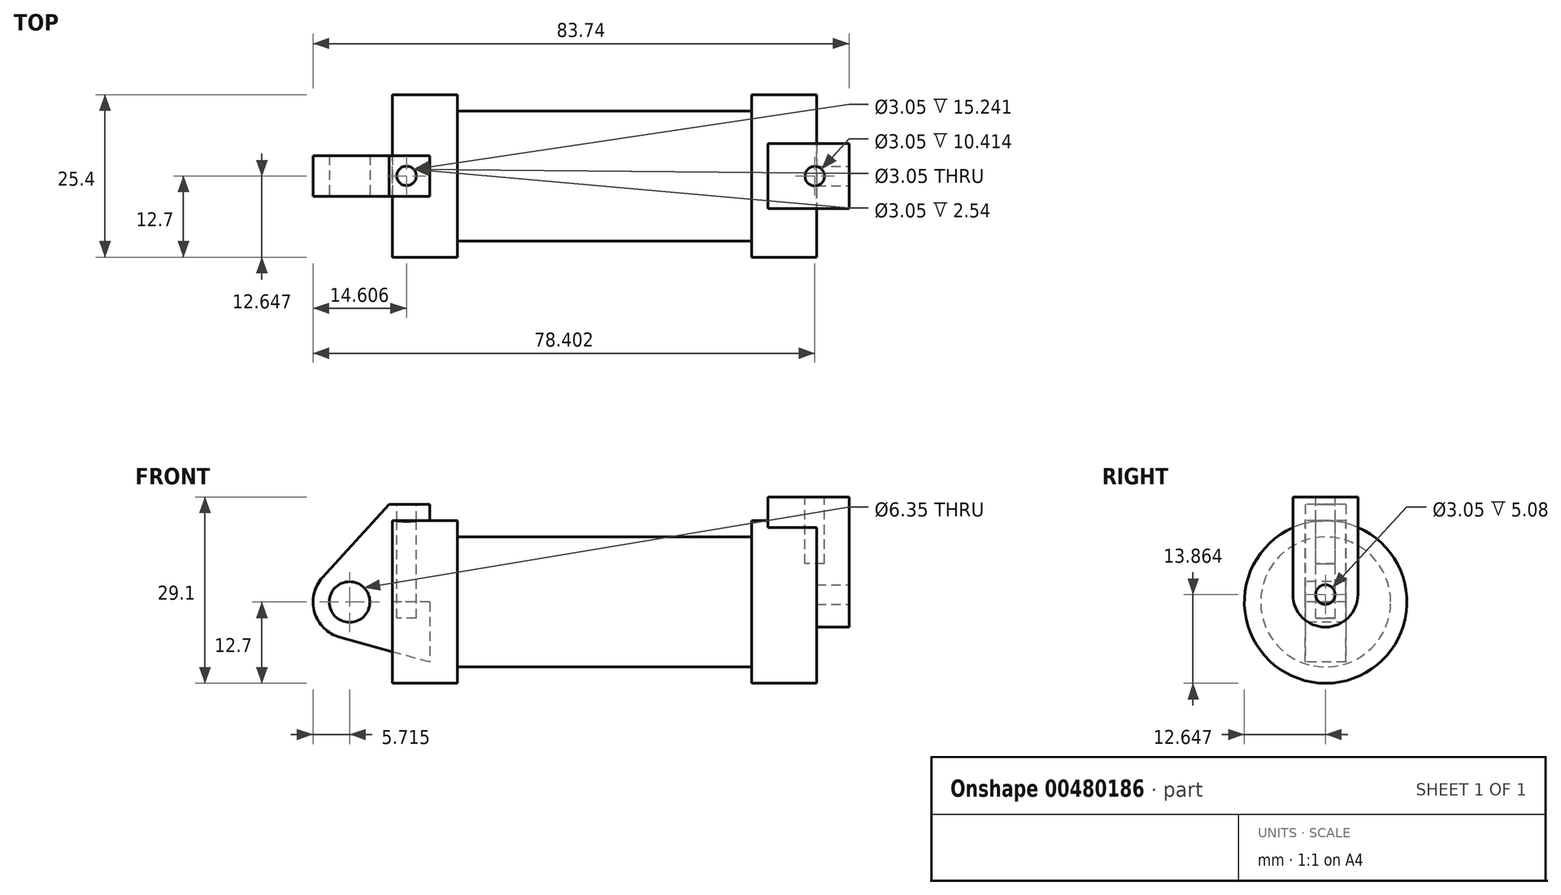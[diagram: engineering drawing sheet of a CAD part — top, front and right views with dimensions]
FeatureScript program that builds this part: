
annotation { "Feature Type Name" : "Feature", "Feature Type Description" : "" }
export const myFeature = defineFeature(function(context is Context, id is Id, definition is map)
    precondition{}
    {
        {
            var Q0;
            Q0=qCreatedBy(makeId("Front.planeOp"),FACE);
            var sketch = newSketch(context, id + "F0", { "sketchPlane" : qUnion([Q0])});
            skLineSegment(sketch, "E0", {"start": v(0, 0) * mm, "end": v(0, 12.7) * mm});
            skLineSegment(sketch, "E1", {"start": v(0, 12.7) * mm, "end": v(10.16, 12.7) * mm});
            skLineSegment(sketch, "E2", {"start": v(10.16, 12.7) * mm, "end": v(10.16, 10.16) * mm});
            skLineSegment(sketch, "E3", {"start": v(10.16, 10.16) * mm, "end": v(56.13, 10.16) * mm});
            skLineSegment(sketch, "E4", {"start": v(56.13, 10.16) * mm, "end": v(56.13, 12.7) * mm});
            skLineSegment(sketch, "E5", {"start": v(56.13, 12.7) * mm, "end": v(66.3, 12.7) * mm});
            skLineSegment(sketch, "E6", {"start": v(66.3, 12.7) * mm, "end": v(66.3, 0) * mm});
            skLineSegment(sketch, "E7", {"start": v(66.3, 0) * mm, "end": v(0, 0) * mm});
            skLineSegment(sketch, "E8", {"start": v(5.84, 15.24) * mm, "end": v(-0.5, 15.24) * mm});
            skLineSegment(sketch, "E9", {"start": v(-0.5, 15.24) * mm, "end": v(-10.88, 3.85) * mm});
            skLineSegment(sketch, "E10", {"start": v(0, 0) * mm, "end": v(-6.65, 0) * mm});
            skCircle(sketch, "E11", {"center": v(-6.65, 0) * mm, "radius": 5.72 * mm});
            skCircle(sketch, "E12", {"center": v(-6.65, 0) * mm, "radius": 3.18 * mm});
            skLineSegment(sketch, "E13", {"start": v(5.84, 15.24) * mm, "end": v(5.84, -9.4) * mm});
            skLineSegment(sketch, "E14", {"start": v(5.84, -9.4) * mm, "end": v(-8.18, -5.5) * mm});
            skSolve(sketch);
        }
        {
            var Q0;
            {var subQ1=sQuery(id+"F0.wireOp",EDGE,"E0");Q0=makeQuery(id+"F0.imprint","IMPRINT",FACE,{"disambiguationData":[TD([[makeQuery(id+"F0.imprint","IMPRINT",EDGE,{"derivedFrom":subQ1}),1.0]])]});}
            var Q1;
            {var subQ5=sQuery(id+"F0.wireOp",EDGE,"E12");Q1=makeQuery(id+"F0.imprint","IMPRINT",FACE,{"disambiguationData":[TD([[makeQuery(id+"F0.imprint","IMPRINT",EDGE,{"derivedFrom":subQ5}),-1.0]])]});}
            var Q2;
            {var subQ0=sQuery(id+"F0.wireOp",EDGE,"E14");Q2=makeQuery(id+"F0.imprint","IMPRINT",FACE,{"disambiguationData":[TD([[makeQuery(id+"F0.imprint","IMPRINT",EDGE,{"derivedFrom":subQ0}),-1.0]])]});}
            extrude(context, id + "F1", {"entities" : qUnion([Q0, Q1, Q2]), "oppositeDirection" : true, "depth" : 3.17 * mm, "hasSecondDirection" : true, "secondDirectionOppositeDirection" : false, "secondDirectionDepth" : 3.17 * mm});
        }
        {
            var Q0;
            {var subQ0=sQuery(id+"F0.wireOp",EDGE,"E0");Q0=makeQuery(id+"F0.imprint","IMPRINT",FACE,{"disambiguationData":[TD([[makeQuery(id+"F0.imprint","IMPRINT",EDGE,{"derivedFrom":subQ0}),-1.0]])]});}
            var Q1;
            {var subQ0=sQuery(id+"F0.wireOp",EDGE,"E2");Q1=makeQuery(id+"F0.imprint","IMPRINT",FACE,{"disambiguationData":[TD([[makeQuery(id+"F0.imprint","IMPRINT",EDGE,{"derivedFrom":subQ0}),-1.0]])]});}
            var Q2;
            Q2=sQuery(id+"F0.wireOp",EDGE,"E7");
            revolve(context, id + "F2", {"entities" : qUnion([Q0, Q1]), "axis" : qUnion([Q2]), "revolveType" : RevolveType.FULL});
        }
        {
            var Q0;
            Q0=makeQuery(id+"F2.opRevolve","SWEPT_FACE",FACE,{"disambiguationData":[OSD([sQuery(id+"F0.wireOp",EDGE,"E6")])]});
            var sketch = newSketch(context, id + "F3", { "sketchPlane" : qUnion([Q0])});
            skCircle(sketch, "E15", {"center": v(-0.05, 1.16) * mm, "radius": 1.52 * mm});
            skCircle(sketch, "E16", {"center": v(-0.05, 1.16) * mm, "radius": 5.08 * mm});
            skLineSegment(sketch, "E17", {"start": v(-5.13, 1.16) * mm, "end": v(-5.13, 16.4) * mm});
            skLineSegment(sketch, "E18", {"start": v(5.03, 1.16) * mm, "end": v(5.03, 16.4) * mm});
            skLineSegment(sketch, "E19", {"start": v(5.03, 16.4) * mm, "end": v(-5.13, 16.4) * mm});
            skSolve(sketch);
        }
        {
            var Q0;
            Q0=makeQuery(id+"F3.imprint","IMPRINT",FACE,{"disambiguationData":[TD([[makeQuery(id+"F3.imprint","IMPRINT",EDGE,{"derivedFrom":sQuery(id+"F3.wireOp",EDGE,"E15")}),-1.0]])]});
            var Q1;
            {var subQ0=sQuery(id+"F3.wireOp",EDGE,"E19");Q1=makeQuery(id+"F3.imprint","IMPRINT",FACE,{"disambiguationData":[TD([[makeQuery(id+"F3.imprint","IMPRINT",EDGE,{"derivedFrom":subQ0}),1.0]])]});}
            var Q2;
            {var subQ0=sQuery(id+"F3.wireOp",EDGE,"E17");var subQ1=sQuery(id+"F3.wireOp",EDGE,"E16");var subQ2=makeQuery(id+"F3.imprint","INTERSECT",VERTEX,{"derivedFrom":[subQ1,subQ0]});Q2=makeQuery(id+"F3.imprint","IMPRINT",FACE,{"disambiguationData":[TD([[makeQuery(id+"F3.imprint","IMPRINT",EDGE,{"disambiguationData":[TD([[subQ2,1.0]])],"derivedFrom":subQ1}),-1.0]])]});}
            extrude(context, id + "F4", {"entities" : qUnion([Q0, Q1, Q2]), "operationType" : NewBodyOperationType.ADD, "oppositeDirection" : true, "depth" : 7.62 * mm, "hasSecondDirection" : true, "secondDirectionOppositeDirection" : false, "secondDirectionDepth" : 5.08 * mm});
        }
        {
            var Q0;
            Q0=makeQuery(id+"F4.opExtrude","SWEPT_FACE",FACE,{"disambiguationData":[OSD([sQuery(id+"F3.wireOp",EDGE,"E19")])]});
            var sketch = newSketch(context, id + "F5", { "sketchPlane" : qUnion([Q0])});
            skCircle(sketch, "E20", {"center": v(66.03, -0.05) * mm, "radius": 1.52 * mm});
            skPoint(sketch, "E20.centerSnap0", {"position": v(71.37, -0.05) * mm});
            skSolve(sketch);
        }
        {
            var Q0;
            Q0=makeQuery(id+"F1.opExtrude","SWEPT_FACE",FACE,{"disambiguationData":[OSD([sQuery(id+"F0.wireOp",EDGE,"E8")])]});
            var sketch = newSketch(context, id + "F6", { "sketchPlane" : qUnion([Q0])});
            skCircle(sketch, "E21", {"center": v(2.24, 0) * mm, "radius": 1.52 * mm});
            skPoint(sketch, "E21.centerSnap0", {"position": v(5.84, 0) * mm});
            skSolve(sketch);
        }
        {
            var Q0;
            Q0=makeQuery(id+"F6.imprint","IMPRINT",FACE,{"disambiguationData":[TD([[makeQuery(id+"F6.imprint","IMPRINT",EDGE,{"derivedFrom":sQuery(id+"F6.wireOp",EDGE,"E21")}),1.0]])]});
            extrude(context, id + "F7", {"entities" : qUnion([Q0]), "operationType" : NewBodyOperationType.REMOVE, "oppositeDirection" : true, "depth" : 17.78 * mm});
        }
        {
            var Q0;
            Q0=makeQuery(id+"F5.imprint","IMPRINT",FACE,{"disambiguationData":[TD([[makeQuery(id+"F5.imprint","IMPRINT",EDGE,{"derivedFrom":sQuery(id+"F5.wireOp",EDGE,"E20")}),1.0]])]});
            extrude(context, id + "F8", {"entities" : qUnion([Q0]), "operationType" : NewBodyOperationType.REMOVE, "oppositeDirection" : true, "depth" : 10.4 * mm});
        }
    });
